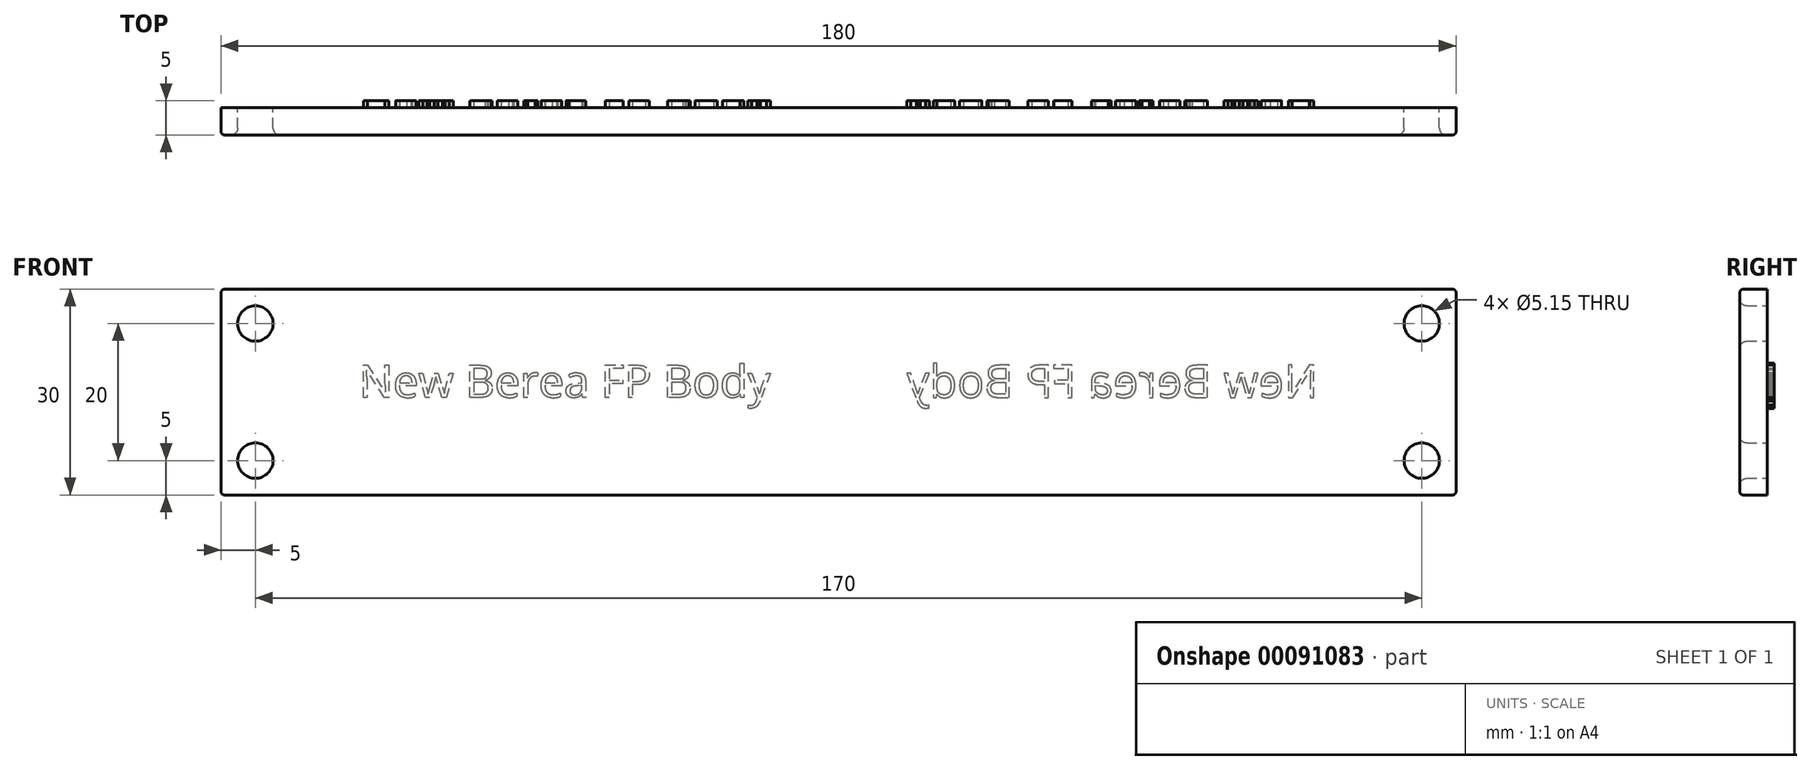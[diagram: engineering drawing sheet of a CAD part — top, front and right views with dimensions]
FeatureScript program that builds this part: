
annotation { "Feature Type Name" : "Feature", "Feature Type Description" : "" }
export const myFeature = defineFeature(function(context is Context, id is Id, definition is map)
    precondition{}
    {
        {
            var Q0;
            Q0=qCreatedBy(makeId("Front.planeOp"),FACE);
            var sketch = newSketch(context, id + "F0", { "sketchPlane" : qUnion([Q0])});
            skLineSegment(sketch, "E0.bottom", {"start": v(-90, -15) * mm, "end": v(90, -15) * mm});
            skLineSegment(sketch, "E0.top", {"start": v(-90, 15) * mm, "end": v(90, 15) * mm});
            skLineSegment(sketch, "E0.left", {"start": v(-90, -15) * mm, "end": v(-90, 15) * mm});
            skLineSegment(sketch, "E0.right", {"start": v(90, -15) * mm, "end": v(90, 15) * mm});
            skPoint(sketch, "E0.middle", {"position": v(0, 0) * mm});
            skCircle(sketch, "E1", {"center": v(-85, 10) * mm, "radius": 2.58 * mm});
            skPoint(sketch, "E2.start.orphan", {"position": v(-90, 0) * mm});
            skPoint(sketch, "E3.orphan", {"position": v(0, 15) * mm});
            skPoint(sketch, "E4.end.orphan", {"position": v(0, -15) * mm});
            skLineSegment(sketch, "E5", {"start": v(-90, 0) * mm, "end": v(0, 0) * mm, "construction": true});
            skLineSegment(sketch, "E6", {"start": v(0, 15) * mm, "end": v(0, -15) * mm, "construction": true});
            skCircle(sketch, "E7.MirrorC", {"center": v(-85, -10) * mm, "radius": 2.58 * mm});
            skCircle(sketch, "E8.MirrorC", {"center": v(85, 10) * mm, "radius": 2.58 * mm});
            skCircle(sketch, "E9.MirrorC", {"center": v(85, -10) * mm, "radius": 2.58 * mm});
            skSolve(sketch);
        }
        {
            var Q0;
            Q0=makeQuery(id+"F0.imprint","IMPRINT",FACE,{"disambiguationData":[TD([[makeQuery(id+"F0.imprint","IMPRINT",EDGE,{"derivedFrom":sQuery(id+"F0.wireOp",EDGE,"E0.bottom")}),1.0]])]});
            extrude(context, id + "F1", {"entities" : qUnion([Q0]), "depth" : 4 * mm});
        }
        {
            var Q0;
            Q0=makeQuery(id+"F1.opExtrude","CAP_EDGE",EDGE,{"disambiguationData":[OSD([sQuery(id+"F0.wireOp",EDGE,"E1")])],"isStart":false});
            var Q1;
            Q1=makeQuery(id+"F1.opExtrude","CAP_EDGE",EDGE,{"disambiguationData":[OSD([sQuery(id+"F0.wireOp",EDGE,"f5b72a5b-8583-449a-bdbf-9ac5a681e1fd0.MirrorC")])],"isStart":false});
            var Q2;
            Q2=makeQuery(id+"F1.opExtrude","CAP_EDGE",EDGE,{"disambiguationData":[OSD([sQuery(id+"F0.wireOp",EDGE,"2623e306-60f4-4522-aa65-1e3e8c2cf5b60.MirrorC")])],"isStart":false});
            var Q3;
            Q3=makeQuery(id+"F1.opExtrude","CAP_EDGE",EDGE,{"disambiguationData":[OSD([sQuery(id+"F0.wireOp",EDGE,"be81a34d-1d50-4ce7-a7a8-4484a1701fac0.MirrorC")])],"isStart":false});
            var Q4;
            Q4=makeQuery(id+"F1.opExtrude","CAP_EDGE",EDGE,{"disambiguationData":[OSD([sQuery(id+"F0.wireOp",EDGE,"E7.MirrorC")])],"isStart":false});
            var Q5;
            Q5=makeQuery(id+"F1.opExtrude","CAP_EDGE",EDGE,{"disambiguationData":[OSD([sQuery(id+"F0.wireOp",EDGE,"E8.MirrorC")])],"isStart":false});
            var Q6;
            Q6=makeQuery(id+"F1.opExtrude","CAP_EDGE",EDGE,{"disambiguationData":[OSD([sQuery(id+"F0.wireOp",EDGE,"E9.MirrorC")])],"isStart":false});
            fillet(context, id + "F2", {"entities" : qUnion([Q0, Q1, Q2, Q3, Q4, Q5, Q6]), "radius" : 1 * mm, "tangentPropagation" : true, "allowEdgeOverflow" : false});
        }
        {
            var Q0;
            Q0=makeQuery(id+"F1.opExtrude","CAP_EDGE",EDGE,{"disambiguationData":[OSD([sQuery(id+"F0.wireOp",EDGE,"E0.top")])],"isStart":false});
            var Q1;
            Q1=makeQuery(id+"F1.opExtrude","CAP_EDGE",EDGE,{"disambiguationData":[OSD([sQuery(id+"F0.wireOp",EDGE,"E0.left")])],"isStart":false});
            var Q2;
            Q2=makeQuery(id+"F1.opExtrude","CAP_EDGE",EDGE,{"disambiguationData":[OSD([sQuery(id+"F0.wireOp",EDGE,"E0.bottom")])],"isStart":false});
            var Q3;
            Q3=makeQuery(id+"F1.opExtrude","CAP_EDGE",EDGE,{"disambiguationData":[OSD([sQuery(id+"F0.wireOp",EDGE,"E0.right")])],"isStart":false});
            var Q4;
            Q4=makeQuery(id+"F1.opExtrude","SWEPT_EDGE",EDGE,{"disambiguationData":[OSD([sQuery(id+"F0.wireOp",EDGE,"E0.top"),sQuery(id+"F0.wireOp",EDGE,"E0.left")])]});
            var Q5;
            Q5=makeQuery(id+"F1.opExtrude","SWEPT_EDGE",EDGE,{"disambiguationData":[OSD([sQuery(id+"F0.wireOp",EDGE,"E0.bottom"),sQuery(id+"F0.wireOp",EDGE,"E0.left")])]});
            var Q6;
            Q6=makeQuery(id+"F1.opExtrude","SWEPT_EDGE",EDGE,{"disambiguationData":[OSD([sQuery(id+"F0.wireOp",EDGE,"E0.top"),sQuery(id+"F0.wireOp",EDGE,"E0.right")])]});
            var Q7;
            Q7=makeQuery(id+"F1.opExtrude","SWEPT_EDGE",EDGE,{"disambiguationData":[OSD([sQuery(id+"F0.wireOp",EDGE,"E0.bottom"),sQuery(id+"F0.wireOp",EDGE,"E0.right")])]});
            fillet(context, id + "F3", {"entities" : qUnion([Q0, Q1, Q2, Q3, Q4, Q5, Q6, Q7]), "radius" : .5 * mm, "tangentPropagation" : true, "allowEdgeOverflow" : false});
        }
        {
            var Q0;
            Q0=makeQuery(id+"F1.opExtrude","CAP_FACE",FACE,{"disambiguationData":[OSD([sQuery(id+"F0.wireOp",EDGE,"E0.bottom"),sQuery(id+"F0.wireOp",EDGE,"E0.top"),sQuery(id+"F0.wireOp",EDGE,"E0.left"),sQuery(id+"F0.wireOp",EDGE,"E0.right"),sQuery(id+"F0.wireOp",EDGE,"E1"),sQuery(id+"F0.wireOp",EDGE,"E7.MirrorC"),sQuery(id+"F0.wireOp",EDGE,"E8.MirrorC"),sQuery(id+"F0.wireOp",EDGE,"E9.MirrorC")])],"isStart":true});
            var sketch = newSketch(context, id + "F4", { "sketchPlane" : qUnion([Q0])});
            skText(sketch, "E10", { "text": "New Berea FP Body\n", "fontName": "OpenSans-Regular.ttf"});
            skLineSegment(sketch, "E11", {"start": v(0, 15) * mm, "end": v(0, -15) * mm, "construction": true});
            const initialGuessF4  = {"E10": [-0.06991, -0.00078, 1, 0, 0.00475]};
            skSetInitialGuess(sketch, initialGuessF4);
            skSolve(sketch);
        }
        {
            var Q0;
            Q0=qSketchRegion(id+"F4",true);
            extrude(context, id + "F5", {"entities" : qUnion([Q0]), "operationType" : NewBodyOperationType.ADD, "depth" : 1 * mm});
        }
        {
            var Q0;
            Q0=makeQuery(id+"F1.opExtrude","SWEPT_BODY",BODY,{"disambiguationData":[OSD([sQuery(id+"F0.wireOp",EDGE,"E0.bottom"),sQuery(id+"F0.wireOp",EDGE,"E0.top"),sQuery(id+"F0.wireOp",EDGE,"E0.left"),sQuery(id+"F0.wireOp",EDGE,"E0.right"),sQuery(id+"F0.wireOp",EDGE,"E1"),sQuery(id+"F0.wireOp",EDGE,"E7.MirrorC"),sQuery(id+"F0.wireOp",EDGE,"E8.MirrorC"),sQuery(id+"F0.wireOp",EDGE,"E9.MirrorC")])]});
            var Q1;
            Q1=makeQuery(id+"F5.opExtrude","SWEPT_FACE",FACE,{"disambiguationData":[OSD([sQuery(id+"F4.wireOp",EDGE,"E10.sketch_text.stroke-94")])]});
            var Q2;
            Q2=makeQuery(id+"F5.opExtrude","SWEPT_FACE",FACE,{"disambiguationData":[OSD([sQuery(id+"F4.wireOp",EDGE,"E10.sketch_text.stroke-169")])]});
            var Q3;
            Q3=makeQuery(id+"F5.opExtrude","SWEPT_FACE",FACE,{"disambiguationData":[OSD([sQuery(id+"F4.wireOp",EDGE,"E10.sketch_text.stroke-185")])]});
            var Q4;
            Q4=makeQuery(id+"F5.opExtrude","SWEPT_FACE",FACE,{"disambiguationData":[OSD([sQuery(id+"F4.wireOp",EDGE,"E10.sketch_text.stroke-125")])]});
            var Q5;
            Q5=makeQuery(id+"F5.opExtrude","SWEPT_FACE",FACE,{"disambiguationData":[OSD([sQuery(id+"F4.wireOp",EDGE,"E10.sketch_text.stroke-155")])]});
            var Q6;
            Q6=makeQuery(id+"F5.opExtrude","SWEPT_FACE",FACE,{"disambiguationData":[OSD([sQuery(id+"F4.wireOp",EDGE,"E10.sketch_text.stroke-65")])]});
            var Q7;
            Q7=makeQuery(id+"F5.opExtrude","SWEPT_FACE",FACE,{"disambiguationData":[OSD([sQuery(id+"F4.wireOp",EDGE,"E10.sketch_text.stroke-81")])]});
            var Q8;
            Q8=makeQuery(id+"F5.opExtrude","SWEPT_FACE",FACE,{"disambiguationData":[OSD([sQuery(id+"F4.wireOp",EDGE,"E10.sketch_text.stroke-67")])]});
            var Q9;
            Q9=makeQuery(id+"F5.opExtrude","SWEPT_FACE",FACE,{"disambiguationData":[OSD([sQuery(id+"F4.wireOp",EDGE,"E10.sketch_text.stroke-99")])]});
            var Q10;
            Q10=makeQuery(id+"F5.opExtrude","SWEPT_FACE",FACE,{"disambiguationData":[OSD([sQuery(id+"F4.wireOp",EDGE,"E10.sketch_text.stroke-127")])]});
            var Q11;
            Q11=makeQuery(id+"F5.opExtrude","SWEPT_FACE",FACE,{"disambiguationData":[OSD([sQuery(id+"F4.wireOp",EDGE,"E10.sketch_text.stroke-10")])]});
            var Q12;
            Q12=makeQuery(id+"F5.opExtrude","CAP_FACE",FACE,{"disambiguationData":[OSD([sQuery(id+"F4.wireOp",EDGE,"E10.sketch_text.stroke-9"),sQuery(id+"F4.wireOp",EDGE,"E10.sketch_text.stroke-10"),sQuery(id+"F4.wireOp",EDGE,"E10.sketch_text.stroke-11"),sQuery(id+"F4.wireOp",EDGE,"E10.sketch_text.stroke-12")])],"isStart":false});
            var Q13;
            Q13=makeQuery(id+"F5.opExtrude","SWEPT_FACE",FACE,{"disambiguationData":[OSD([sQuery(id+"F4.wireOp",EDGE,"E10.sketch_text.stroke-154")])]});
            var Q14;
            Q14=makeQuery(id+"F5.opExtrude","SWEPT_FACE",FACE,{"disambiguationData":[OSD([sQuery(id+"F4.wireOp",EDGE,"E10.sketch_text.stroke-1")])]});
            var Q15;
            Q15=makeQuery(id+"F5.opExtrude","CAP_FACE",FACE,{"disambiguationData":[OSD([sQuery(id+"F4.wireOp",EDGE,"E10.sketch_text.stroke-124"),sQuery(id+"F4.wireOp",EDGE,"E10.sketch_text.stroke-125"),sQuery(id+"F4.wireOp",EDGE,"E10.sketch_text.stroke-126"),sQuery(id+"F4.wireOp",EDGE,"E10.sketch_text.stroke-127"),sQuery(id+"F4.wireOp",EDGE,"E10.sketch_text.stroke-128"),sQuery(id+"F4.wireOp",EDGE,"E10.sketch_text.stroke-129"),sQuery(id+"F4.wireOp",EDGE,"E10.sketch_text.stroke-130"),sQuery(id+"F4.wireOp",EDGE,"E10.sketch_text.stroke-131"),sQuery(id+"F4.wireOp",EDGE,"E10.sketch_text.stroke-132"),sQuery(id+"F4.wireOp",EDGE,"E10.sketch_text.stroke-133"),sQuery(id+"F4.wireOp",EDGE,"E10.sketch_text.stroke-134"),sQuery(id+"F4.wireOp",EDGE,"E10.sketch_text.stroke-135"),sQuery(id+"F4.wireOp",EDGE,"E10.sketch_text.stroke-136"),sQuery(id+"F4.wireOp",EDGE,"E10.sketch_text.stroke-137"),sQuery(id+"F4.wireOp",EDGE,"E10.sketch_text.stroke-138")])],"isStart":false});
            var Q16;
            Q16=makeQuery(id+"F5.opExtrude","CAP_FACE",FACE,{"disambiguationData":[OSD([sQuery(id+"F4.wireOp",EDGE,"E10.sketch_text.stroke-34"),sQuery(id+"F4.wireOp",EDGE,"E10.sketch_text.stroke-35"),sQuery(id+"F4.wireOp",EDGE,"E10.sketch_text.stroke-36"),sQuery(id+"F4.wireOp",EDGE,"E10.sketch_text.stroke-37"),sQuery(id+"F4.wireOp",EDGE,"E10.sketch_text.stroke-38"),sQuery(id+"F4.wireOp",EDGE,"E10.sketch_text.stroke-39"),sQuery(id+"F4.wireOp",EDGE,"E10.sketch_text.stroke-40"),sQuery(id+"F4.wireOp",EDGE,"E10.sketch_text.stroke-41"),sQuery(id+"F4.wireOp",EDGE,"E10.sketch_text.stroke-42"),sQuery(id+"F4.wireOp",EDGE,"E10.sketch_text.stroke-43"),sQuery(id+"F4.wireOp",EDGE,"E10.sketch_text.stroke-44"),sQuery(id+"F4.wireOp",EDGE,"E10.sketch_text.stroke-45"),sQuery(id+"F4.wireOp",EDGE,"E10.sketch_text.stroke-46"),sQuery(id+"F4.wireOp",EDGE,"E10.sketch_text.stroke-47"),sQuery(id+"F4.wireOp",EDGE,"E10.sketch_text.stroke-48"),sQuery(id+"F4.wireOp",EDGE,"E10.sketch_text.stroke-49"),sQuery(id+"F4.wireOp",EDGE,"E10.sketch_text.stroke-50"),sQuery(id+"F4.wireOp",EDGE,"E10.sketch_text.stroke-51"),sQuery(id+"F4.wireOp",EDGE,"E10.sketch_text.stroke-52"),sQuery(id+"F4.wireOp",EDGE,"E10.sketch_text.stroke-53"),sQuery(id+"F4.wireOp",EDGE,"E10.sketch_text.stroke-54"),sQuery(id+"F4.wireOp",EDGE,"E10.sketch_text.stroke-55"),sQuery(id+"F4.wireOp",EDGE,"E10.sketch_text.stroke-56"),sQuery(id+"F4.wireOp",EDGE,"E10.sketch_text.stroke-57"),sQuery(id+"F4.wireOp",EDGE,"E10.sketch_text.stroke-58"),sQuery(id+"F4.wireOp",EDGE,"E10.sketch_text.stroke-59"),sQuery(id+"F4.wireOp",EDGE,"E10.sketch_text.stroke-60")])],"isStart":false});
            var Q17;
            Q17=makeQuery(id+"F5.opExtrude","SWEPT_FACE",FACE,{"disambiguationData":[OSD([sQuery(id+"F4.wireOp",EDGE,"E10.sketch_text.stroke-50")])]});
            var Q18;
            Q18=makeQuery(id+"F5.opExtrude","SWEPT_FACE",FACE,{"disambiguationData":[OSD([sQuery(id+"F4.wireOp",EDGE,"E10.sketch_text.stroke-2")])]});
            var Q19;
            Q19=makeQuery(id+"F5.opExtrude","SWEPT_FACE",FACE,{"disambiguationData":[OSD([sQuery(id+"F4.wireOp",EDGE,"E10.sketch_text.stroke-3")])]});
            var Q20;
            Q20=makeQuery(id+"F5.opExtrude","SWEPT_FACE",FACE,{"disambiguationData":[OSD([sQuery(id+"F4.wireOp",EDGE,"E10.sketch_text.stroke-5")])]});
            var Q21;
            Q21=makeQuery(id+"F5.opExtrude","SWEPT_FACE",FACE,{"disambiguationData":[OSD([sQuery(id+"F4.wireOp",EDGE,"E10.sketch_text.stroke-8")])]});
            var Q22;
            Q22=makeQuery(id+"F5.opExtrude","SWEPT_FACE",FACE,{"disambiguationData":[OSD([sQuery(id+"F4.wireOp",EDGE,"E10.sketch_text.stroke-98")])]});
            var Q23;
            Q23=makeQuery(id+"F5.opExtrude","SWEPT_FACE",FACE,{"disambiguationData":[OSD([sQuery(id+"F4.wireOp",EDGE,"E10.sketch_text.stroke-66")])]});
            var Q24;
            Q24=makeQuery(id+"F5.opExtrude","SWEPT_FACE",FACE,{"disambiguationData":[OSD([sQuery(id+"F4.wireOp",EDGE,"E10.sketch_text.stroke-153")])]});
            var Q25;
            Q25=makeQuery(id+"F5.opExtrude","SWEPT_FACE",FACE,{"disambiguationData":[OSD([sQuery(id+"F4.wireOp",EDGE,"E10.sketch_text.stroke-126")])]});
            var Q26;
            Q26=makeQuery(id+"F5.opExtrude","SWEPT_FACE",FACE,{"disambiguationData":[OSD([sQuery(id+"F4.wireOp",EDGE,"E10.sketch_text.stroke-183")])]});
            var Q27;
            Q27=makeQuery(id+"F5.opExtrude","SWEPT_FACE",FACE,{"disambiguationData":[OSD([sQuery(id+"F4.wireOp",EDGE,"E10.sketch_text.stroke-109")])]});
            var Q28;
            Q28=makeQuery(id+"F5.opExtrude","SWEPT_FACE",FACE,{"disambiguationData":[OSD([sQuery(id+"F4.wireOp",EDGE,"E10.sketch_text.stroke-186")])]});
            var Q29;
            Q29=makeQuery(id+"F5.opExtrude","SWEPT_FACE",FACE,{"disambiguationData":[OSD([sQuery(id+"F4.wireOp",EDGE,"E10.sketch_text.stroke-79")])]});
            var Q30;
            Q30=makeQuery(id+"F5.opExtrude","SWEPT_FACE",FACE,{"disambiguationData":[OSD([sQuery(id+"F4.wireOp",EDGE,"E10.sketch_text.stroke-110")])]});
            var Q31;
            Q31=makeQuery(id+"F5.opExtrude","SWEPT_FACE",FACE,{"disambiguationData":[OSD([sQuery(id+"F4.wireOp",EDGE,"E10.sketch_text.stroke-38")])]});
            var Q32;
            Q32=makeQuery(id+"F5.opExtrude","SWEPT_FACE",FACE,{"disambiguationData":[OSD([sQuery(id+"F4.wireOp",EDGE,"E10.sketch_text.stroke-24")])]});
            var Q33;
            Q33=makeQuery(id+"F5.opExtrude","SWEPT_FACE",FACE,{"disambiguationData":[OSD([sQuery(id+"F4.wireOp",EDGE,"E10.sketch_text.stroke-12")])]});
            var Q34;
            Q34=makeQuery(id+"F5.opExtrude","SWEPT_FACE",FACE,{"disambiguationData":[OSD([sQuery(id+"F4.wireOp",EDGE,"E10.sketch_text.stroke-100")])]});
            var Q35;
            Q35=makeQuery(id+"F5.opExtrude","SWEPT_FACE",FACE,{"disambiguationData":[OSD([sQuery(id+"F4.wireOp",EDGE,"E10.sketch_text.stroke-158")])]});
            var Q36;
            Q36=makeQuery(id+"F5.opExtrude","SWEPT_FACE",FACE,{"disambiguationData":[OSD([sQuery(id+"F4.wireOp",EDGE,"E10.sketch_text.stroke-142")])]});
            var Q37;
            Q37=makeQuery(id+"F5.opExtrude","SWEPT_FACE",FACE,{"disambiguationData":[OSD([sQuery(id+"F4.wireOp",EDGE,"E10.sketch_text.stroke-54")])]});
            var Q38;
            Q38=makeQuery(id+"F5.opExtrude","SWEPT_FACE",FACE,{"disambiguationData":[OSD([sQuery(id+"F4.wireOp",EDGE,"E10.sketch_text.stroke-25")])]});
            var Q39;
            Q39=makeQuery(id+"F5.opExtrude","SWEPT_FACE",FACE,{"disambiguationData":[OSD([sQuery(id+"F4.wireOp",EDGE,"E10.sketch_text.stroke-101")])]});
            var Q40;
            Q40=makeQuery(id+"F5.opExtrude","SWEPT_FACE",FACE,{"disambiguationData":[OSD([sQuery(id+"F4.wireOp",EDGE,"E10.sketch_text.stroke-69")])]});
            var Q41;
            Q41=makeQuery(id+"F5.opExtrude","SWEPT_FACE",FACE,{"disambiguationData":[OSD([sQuery(id+"F4.wireOp",EDGE,"E10.sketch_text.stroke-159")])]});
            var Q42;
            Q42=makeQuery(id+"F5.opExtrude","SWEPT_FACE",FACE,{"disambiguationData":[OSD([sQuery(id+"F4.wireOp",EDGE,"E10.sketch_text.stroke-85")])]});
            var Q43;
            Q43=makeQuery(id+"F5.opExtrude","SWEPT_FACE",FACE,{"disambiguationData":[OSD([sQuery(id+"F4.wireOp",EDGE,"E10.sketch_text.stroke-173")])]});
            var Q44;
            Q44=makeQuery(id+"F5.opExtrude","SWEPT_FACE",FACE,{"disambiguationData":[OSD([sQuery(id+"F4.wireOp",EDGE,"E10.sketch_text.stroke-40")])]});
            var Q45;
            Q45=makeQuery(id+"F5.opExtrude","SWEPT_FACE",FACE,{"disambiguationData":[OSD([sQuery(id+"F4.wireOp",EDGE,"E10.sketch_text.stroke-102")])]});
            var Q46;
            Q46=makeQuery(id+"F5.opExtrude","SWEPT_FACE",FACE,{"disambiguationData":[OSD([sQuery(id+"F4.wireOp",EDGE,"E10.sketch_text.stroke-86")])]});
            var Q47;
            Q47=makeQuery(id+"F5.opExtrude","SWEPT_FACE",FACE,{"disambiguationData":[OSD([sQuery(id+"F4.wireOp",EDGE,"E10.sketch_text.stroke-130")])]});
            var Q48;
            Q48=makeQuery(id+"F5.opExtrude","SWEPT_FACE",FACE,{"disambiguationData":[OSD([sQuery(id+"F4.wireOp",EDGE,"E10.sketch_text.stroke-103")])]});
            var Q49;
            Q49=makeQuery(id+"F5.opExtrude","SWEPT_FACE",FACE,{"disambiguationData":[OSD([sQuery(id+"F4.wireOp",EDGE,"E10.sketch_text.stroke-87")])]});
            var Q50;
            Q50=makeQuery(id+"F5.opExtrude","SWEPT_FACE",FACE,{"disambiguationData":[OSD([sQuery(id+"F4.wireOp",EDGE,"E10.sketch_text.stroke-145")])]});
            var Q51;
            Q51=makeQuery(id+"F5.opExtrude","SWEPT_FACE",FACE,{"disambiguationData":[OSD([sQuery(id+"F4.wireOp",EDGE,"E10.sketch_text.stroke-131")])]});
            var Q52;
            Q52=makeQuery(id+"F5.opExtrude","SWEPT_FACE",FACE,{"disambiguationData":[OSD([sQuery(id+"F4.wireOp",EDGE,"E10.sketch_text.stroke-28")])]});
            var Q53;
            Q53=makeQuery(id+"F5.opExtrude","SWEPT_FACE",FACE,{"disambiguationData":[OSD([sQuery(id+"F4.wireOp",EDGE,"E10.sketch_text.stroke-14")])]});
            var Q54;
            Q54=makeQuery(id+"F5.opExtrude","SWEPT_FACE",FACE,{"disambiguationData":[OSD([sQuery(id+"F4.wireOp",EDGE,"E10.sketch_text.stroke-88")])]});
            var Q55;
            Q55=makeQuery(id+"F5.opExtrude","SWEPT_FACE",FACE,{"disambiguationData":[OSD([sQuery(id+"F4.wireOp",EDGE,"E10.sketch_text.stroke-162")])]});
            var Q56;
            Q56=makeQuery(id+"F5.opExtrude","SWEPT_FACE",FACE,{"disambiguationData":[OSD([sQuery(id+"F4.wireOp",EDGE,"E10.sketch_text.stroke-176")])]});
            var Q57;
            Q57=makeQuery(id+"F5.opExtrude","SWEPT_FACE",FACE,{"disambiguationData":[OSD([sQuery(id+"F4.wireOp",EDGE,"E10.sketch_text.stroke-73")])]});
            var Q58;
            Q58=makeQuery(id+"F5.opExtrude","SWEPT_FACE",FACE,{"disambiguationData":[OSD([sQuery(id+"F4.wireOp",EDGE,"E10.sketch_text.stroke-59")])]});
            var Q59;
            Q59=makeQuery(id+"F5.opExtrude","SWEPT_FACE",FACE,{"disambiguationData":[OSD([sQuery(id+"F4.wireOp",EDGE,"E10.sketch_text.stroke-133")])]});
            var Q60;
            Q60=makeQuery(id+"F5.opExtrude","SWEPT_FACE",FACE,{"disambiguationData":[OSD([sQuery(id+"F4.wireOp",EDGE,"E10.sketch_text.stroke-119")])]});
            var Q61;
            Q61=makeQuery(id+"F5.opExtrude","SWEPT_FACE",FACE,{"disambiguationData":[OSD([sQuery(id+"F4.wireOp",EDGE,"E10.sketch_text.stroke-74")])]});
            var Q62;
            Q62=makeQuery(id+"F5.opExtrude","SWEPT_FACE",FACE,{"disambiguationData":[OSD([sQuery(id+"F4.wireOp",EDGE,"E10.sketch_text.stroke-44")])]});
            var Q63;
            Q63=makeQuery(id+"F5.opExtrude","SWEPT_FACE",FACE,{"disambiguationData":[OSD([sQuery(id+"F4.wireOp",EDGE,"E10.sketch_text.stroke-120")])]});
            var Q64;
            Q64=makeQuery(id+"F5.opExtrude","SWEPT_FACE",FACE,{"disambiguationData":[OSD([sQuery(id+"F4.wireOp",EDGE,"E10.sketch_text.stroke-90")])]});
            var Q65;
            Q65=makeQuery(id+"F5.opExtrude","SWEPT_FACE",FACE,{"disambiguationData":[OSD([sQuery(id+"F4.wireOp",EDGE,"E10.sketch_text.stroke-178")])]});
            var Q66;
            Q66=makeQuery(id+"F5.opExtrude","SWEPT_FACE",FACE,{"disambiguationData":[OSD([sQuery(id+"F4.wireOp",EDGE,"E10.sketch_text.stroke-45")])]});
            var Q67;
            Q67=makeQuery(id+"F5.opExtrude","SWEPT_FACE",FACE,{"disambiguationData":[OSD([sQuery(id+"F4.wireOp",EDGE,"E10.sketch_text.stroke-31")])]});
            var Q68;
            Q68=makeQuery(id+"F5.opExtrude","SWEPT_FACE",FACE,{"disambiguationData":[OSD([sQuery(id+"F4.wireOp",EDGE,"E10.sketch_text.stroke-135")])]});
            var Q69;
            Q69=makeQuery(id+"F5.opExtrude","SWEPT_FACE",FACE,{"disambiguationData":[OSD([sQuery(id+"F4.wireOp",EDGE,"E10.sketch_text.stroke-179")])]});
            var Q70;
            Q70=makeQuery(id+"F5.opExtrude","SWEPT_FACE",FACE,{"disambiguationData":[OSD([sQuery(id+"F4.wireOp",EDGE,"E10.sketch_text.stroke-165")])]});
            var Q71;
            Q71=makeQuery(id+"F5.opExtrude","SWEPT_FACE",FACE,{"disambiguationData":[OSD([sQuery(id+"F4.wireOp",EDGE,"E10.sketch_text.stroke-149")])]});
            var Q72;
            Q72=makeQuery(id+"F5.opExtrude","SWEPT_FACE",FACE,{"disambiguationData":[OSD([sQuery(id+"F4.wireOp",EDGE,"E10.sketch_text.stroke-136")])]});
            var Q73;
            Q73=makeQuery(id+"F5.opExtrude","SWEPT_FACE",FACE,{"disambiguationData":[OSD([sQuery(id+"F4.wireOp",EDGE,"E10.sketch_text.stroke-122")])]});
            var Q74;
            Q74=makeQuery(id+"F5.opExtrude","SWEPT_FACE",FACE,{"disambiguationData":[OSD([sQuery(id+"F4.wireOp",EDGE,"E10.sketch_text.stroke-106")])]});
            var Q75;
            Q75=makeQuery(id+"F5.opExtrude","SWEPT_FACE",FACE,{"disambiguationData":[OSD([sQuery(id+"F4.wireOp",EDGE,"E10.sketch_text.stroke-180")])]});
            var Q76;
            Q76=makeQuery(id+"F5.opExtrude","SWEPT_FACE",FACE,{"disambiguationData":[OSD([sQuery(id+"F4.wireOp",EDGE,"E10.sketch_text.stroke-166")])]});
            var Q77;
            Q77=makeQuery(id+"F5.opExtrude","SWEPT_FACE",FACE,{"disambiguationData":[OSD([sQuery(id+"F4.wireOp",EDGE,"E10.sketch_text.stroke-150")])]});
            var Q78;
            Q78=makeQuery(id+"F5.opExtrude","SWEPT_FACE",FACE,{"disambiguationData":[OSD([sQuery(id+"F4.wireOp",EDGE,"E10.sketch_text.stroke-76")])]});
            var Q79;
            Q79=makeQuery(id+"F5.opExtrude","SWEPT_FACE",FACE,{"disambiguationData":[OSD([sQuery(id+"F4.wireOp",EDGE,"E10.sketch_text.stroke-32")])]});
            var Q80;
            Q80=makeQuery(id+"F5.opExtrude","SWEPT_FACE",FACE,{"disambiguationData":[OSD([sQuery(id+"F4.wireOp",EDGE,"E10.sketch_text.stroke-181")])]});
            var Q81;
            Q81=makeQuery(id+"F5.opExtrude","SWEPT_FACE",FACE,{"disambiguationData":[OSD([sQuery(id+"F4.wireOp",EDGE,"E10.sketch_text.stroke-47")])]});
            var Q82;
            Q82=makeQuery(id+"F5.opExtrude","SWEPT_FACE",FACE,{"disambiguationData":[OSD([sQuery(id+"F4.wireOp",EDGE,"E10.sketch_text.stroke-123")])]});
            var Q83;
            Q83=makeQuery(id+"F5.opExtrude","SWEPT_FACE",FACE,{"disambiguationData":[OSD([sQuery(id+"F4.wireOp",EDGE,"E10.sketch_text.stroke-107")])]});
            var Q84;
            Q84=makeQuery(id+"F5.opExtrude","SWEPT_FACE",FACE,{"disambiguationData":[OSD([sQuery(id+"F4.wireOp",EDGE,"E10.sketch_text.stroke-48")])]});
            var Q85;
            Q85=makeQuery(id+"F5.opExtrude","SWEPT_FACE",FACE,{"disambiguationData":[OSD([sQuery(id+"F4.wireOp",EDGE,"E10.sketch_text.stroke-124")])]});
            var Q86;
            Q86=makeQuery(id+"F5.opExtrude","SWEPT_FACE",FACE,{"disambiguationData":[OSD([sQuery(id+"F4.wireOp",EDGE,"E10.sketch_text.stroke-108")])]});
            var Q87;
            Q87=makeQuery(id+"F5.opExtrude","CAP_FACE",FACE,{"disambiguationData":[OSD([sQuery(id+"F4.wireOp",EDGE,"E10.sketch_text.stroke-139"),sQuery(id+"F4.wireOp",EDGE,"E10.sketch_text.stroke-140"),sQuery(id+"F4.wireOp",EDGE,"E10.sketch_text.stroke-141"),sQuery(id+"F4.wireOp",EDGE,"E10.sketch_text.stroke-142"),sQuery(id+"F4.wireOp",EDGE,"E10.sketch_text.stroke-143"),sQuery(id+"F4.wireOp",EDGE,"E10.sketch_text.stroke-144"),sQuery(id+"F4.wireOp",EDGE,"E10.sketch_text.stroke-145"),sQuery(id+"F4.wireOp",EDGE,"E10.sketch_text.stroke-146"),sQuery(id+"F4.wireOp",EDGE,"E10.sketch_text.stroke-147"),sQuery(id+"F4.wireOp",EDGE,"E10.sketch_text.stroke-148"),sQuery(id+"F4.wireOp",EDGE,"E10.sketch_text.stroke-149"),sQuery(id+"F4.wireOp",EDGE,"E10.sketch_text.stroke-150"),sQuery(id+"F4.wireOp",EDGE,"E10.sketch_text.stroke-151"),sQuery(id+"F4.wireOp",EDGE,"E10.sketch_text.stroke-152"),sQuery(id+"F4.wireOp",EDGE,"E10.sketch_text.stroke-153"),sQuery(id+"F4.wireOp",EDGE,"E10.sketch_text.stroke-154"),sQuery(id+"F4.wireOp",EDGE,"E10.sketch_text.stroke-155"),sQuery(id+"F4.wireOp",EDGE,"E10.sketch_text.stroke-156"),sQuery(id+"F4.wireOp",EDGE,"E10.sketch_text.stroke-157"),sQuery(id+"F4.wireOp",EDGE,"E10.sketch_text.stroke-158"),sQuery(id+"F4.wireOp",EDGE,"E10.sketch_text.stroke-159"),sQuery(id+"F4.wireOp",EDGE,"E10.sketch_text.stroke-160"),sQuery(id+"F4.wireOp",EDGE,"E10.sketch_text.stroke-161"),sQuery(id+"F4.wireOp",EDGE,"E10.sketch_text.stroke-162"),sQuery(id+"F4.wireOp",EDGE,"E10.sketch_text.stroke-163"),sQuery(id+"F4.wireOp",EDGE,"E10.sketch_text.stroke-164"),sQuery(id+"F4.wireOp",EDGE,"E10.sketch_text.stroke-165")])],"isStart":false});
            var Q88;
            Q88=makeQuery(id+"F5.opExtrude","CAP_FACE",FACE,{"disambiguationData":[OSD([sQuery(id+"F4.wireOp",EDGE,"E10.sketch_text.stroke-21"),sQuery(id+"F4.wireOp",EDGE,"E10.sketch_text.stroke-22"),sQuery(id+"F4.wireOp",EDGE,"E10.sketch_text.stroke-23"),sQuery(id+"F4.wireOp",EDGE,"E10.sketch_text.stroke-24"),sQuery(id+"F4.wireOp",EDGE,"E10.sketch_text.stroke-25"),sQuery(id+"F4.wireOp",EDGE,"E10.sketch_text.stroke-26"),sQuery(id+"F4.wireOp",EDGE,"E10.sketch_text.stroke-27"),sQuery(id+"F4.wireOp",EDGE,"E10.sketch_text.stroke-28"),sQuery(id+"F4.wireOp",EDGE,"E10.sketch_text.stroke-29"),sQuery(id+"F4.wireOp",EDGE,"E10.sketch_text.stroke-30"),sQuery(id+"F4.wireOp",EDGE,"E10.sketch_text.stroke-31"),sQuery(id+"F4.wireOp",EDGE,"E10.sketch_text.stroke-32"),sQuery(id+"F4.wireOp",EDGE,"E10.sketch_text.stroke-33")])],"isStart":false});
            var Q89;
            Q89=makeQuery(id+"F5.opExtrude","SWEPT_FACE",FACE,{"disambiguationData":[OSD([sQuery(id+"F4.wireOp",EDGE,"E10.sketch_text.stroke-113")])]});
            var Q90;
            Q90=makeQuery(id+"F5.opExtrude","SWEPT_FACE",FACE,{"disambiguationData":[OSD([sQuery(id+"F4.wireOp",EDGE,"E10.sketch_text.stroke-37")])]});
            var Q91;
            Q91=makeQuery(id+"F5.opExtrude","SWEPT_FACE",FACE,{"disambiguationData":[OSD([sQuery(id+"F4.wireOp",EDGE,"E10.sketch_text.stroke-187")])]});
            var Q92;
            Q92=makeQuery(id+"F5.opExtrude","SWEPT_FACE",FACE,{"disambiguationData":[OSD([sQuery(id+"F4.wireOp",EDGE,"E10.sketch_text.stroke-0")])]});
            var Q93;
            Q93=makeQuery(id+"F5.opExtrude","SWEPT_FACE",FACE,{"disambiguationData":[OSD([sQuery(id+"F4.wireOp",EDGE,"E10.sketch_text.stroke-4")])]});
            var Q94;
            Q94=makeQuery(id+"F5.opExtrude","SWEPT_FACE",FACE,{"disambiguationData":[OSD([sQuery(id+"F4.wireOp",EDGE,"E10.sketch_text.stroke-82")])]});
            var Q95;
            Q95=makeQuery(id+"F5.opExtrude","SWEPT_FACE",FACE,{"disambiguationData":[OSD([sQuery(id+"F4.wireOp",EDGE,"E10.sketch_text.stroke-52")])]});
            var Q96;
            Q96=makeQuery(id+"F5.opExtrude","SWEPT_FACE",FACE,{"disambiguationData":[OSD([sQuery(id+"F4.wireOp",EDGE,"E10.sketch_text.stroke-49")])]});
            var Q97;
            Q97=makeQuery(id+"F5.opExtrude","SWEPT_FACE",FACE,{"disambiguationData":[OSD([sQuery(id+"F4.wireOp",EDGE,"E10.sketch_text.stroke-63")])]});
            var Q98;
            Q98=makeQuery(id+"F5.opExtrude","SWEPT_FACE",FACE,{"disambiguationData":[OSD([sQuery(id+"F4.wireOp",EDGE,"E10.sketch_text.stroke-21")])]});
            var Q99;
            Q99=makeQuery(id+"F5.opExtrude","SWEPT_FACE",FACE,{"disambiguationData":[OSD([sQuery(id+"F4.wireOp",EDGE,"E10.sketch_text.stroke-128")])]});
            var Q100;
            Q100=makeQuery(id+"F5.opExtrude","SWEPT_FACE",FACE,{"disambiguationData":[OSD([sQuery(id+"F4.wireOp",EDGE,"E10.sketch_text.stroke-55")])]});
            var Q101;
            Q101=makeQuery(id+"F5.opExtrude","SWEPT_FACE",FACE,{"disambiguationData":[OSD([sQuery(id+"F4.wireOp",EDGE,"E10.sketch_text.stroke-26")])]});
            var Q102;
            Q102=makeQuery(id+"F5.opExtrude","SWEPT_FACE",FACE,{"disambiguationData":[OSD([sQuery(id+"F4.wireOp",EDGE,"E10.sketch_text.stroke-174")])]});
            var Q103;
            Q103=makeQuery(id+"F5.opExtrude","SWEPT_FACE",FACE,{"disambiguationData":[OSD([sQuery(id+"F4.wireOp",EDGE,"E10.sketch_text.stroke-104")])]});
            var Q104;
            Q104=makeQuery(id+"F5.opExtrude","SWEPT_FACE",FACE,{"disambiguationData":[OSD([sQuery(id+"F4.wireOp",EDGE,"E10.sketch_text.stroke-72")])]});
            var Q105;
            Q105=makeQuery(id+"F5.opExtrude","SWEPT_FACE",FACE,{"disambiguationData":[OSD([sQuery(id+"F4.wireOp",EDGE,"E10.sketch_text.stroke-132")])]});
            var Q106;
            Q106=makeQuery(id+"F5.opExtrude","SWEPT_FACE",FACE,{"disambiguationData":[OSD([sQuery(id+"F4.wireOp",EDGE,"E10.sketch_text.stroke-43")])]});
            var Q107;
            Q107=makeQuery(id+"F5.opExtrude","SWEPT_FACE",FACE,{"disambiguationData":[OSD([sQuery(id+"F4.wireOp",EDGE,"E10.sketch_text.stroke-15")])]});
            var Q108;
            Q108=makeQuery(id+"F5.opExtrude","SWEPT_FACE",FACE,{"disambiguationData":[OSD([sQuery(id+"F4.wireOp",EDGE,"E10.sketch_text.stroke-89")])]});
            var Q109;
            Q109=makeQuery(id+"F5.opExtrude","SWEPT_FACE",FACE,{"disambiguationData":[OSD([sQuery(id+"F4.wireOp",EDGE,"E10.sketch_text.stroke-163")])]});
            var Q110;
            Q110=makeQuery(id+"F5.opExtrude","SWEPT_FACE",FACE,{"disambiguationData":[OSD([sQuery(id+"F4.wireOp",EDGE,"E10.sketch_text.stroke-30")])]});
            var Q111;
            Q111=makeQuery(id+"F5.opExtrude","SWEPT_FACE",FACE,{"disambiguationData":[OSD([sQuery(id+"F4.wireOp",EDGE,"E10.sketch_text.stroke-134")])]});
            var Q112;
            Q112=makeQuery(id+"F5.opExtrude","SWEPT_FACE",FACE,{"disambiguationData":[OSD([sQuery(id+"F4.wireOp",EDGE,"E10.sketch_text.stroke-121")])]});
            var Q113;
            Q113=makeQuery(id+"F5.opExtrude","CAP_FACE",FACE,{"disambiguationData":[OSD([sQuery(id+"F4.wireOp",EDGE,"E10.sketch_text.stroke-105"),sQuery(id+"F4.wireOp",EDGE,"E10.sketch_text.stroke-106"),sQuery(id+"F4.wireOp",EDGE,"E10.sketch_text.stroke-107"),sQuery(id+"F4.wireOp",EDGE,"E10.sketch_text.stroke-108"),sQuery(id+"F4.wireOp",EDGE,"E10.sketch_text.stroke-109"),sQuery(id+"F4.wireOp",EDGE,"E10.sketch_text.stroke-110"),sQuery(id+"F4.wireOp",EDGE,"E10.sketch_text.stroke-111"),sQuery(id+"F4.wireOp",EDGE,"E10.sketch_text.stroke-112"),sQuery(id+"F4.wireOp",EDGE,"E10.sketch_text.stroke-113"),sQuery(id+"F4.wireOp",EDGE,"E10.sketch_text.stroke-114"),sQuery(id+"F4.wireOp",EDGE,"E10.sketch_text.stroke-115"),sQuery(id+"F4.wireOp",EDGE,"E10.sketch_text.stroke-116"),sQuery(id+"F4.wireOp",EDGE,"E10.sketch_text.stroke-117"),sQuery(id+"F4.wireOp",EDGE,"E10.sketch_text.stroke-118"),sQuery(id+"F4.wireOp",EDGE,"E10.sketch_text.stroke-119"),sQuery(id+"F4.wireOp",EDGE,"E10.sketch_text.stroke-120"),sQuery(id+"F4.wireOp",EDGE,"E10.sketch_text.stroke-121"),sQuery(id+"F4.wireOp",EDGE,"E10.sketch_text.stroke-122"),sQuery(id+"F4.wireOp",EDGE,"E10.sketch_text.stroke-123")])],"isStart":false});
            var Q114;
            Q114=makeQuery(id+"F5.opExtrude","SWEPT_FACE",FACE,{"disambiguationData":[OSD([sQuery(id+"F4.wireOp",EDGE,"E10.sketch_text.stroke-92")])]});
            var Q115;
            Q115=makeQuery(id+"F5.opExtrude","SWEPT_FACE",FACE,{"disambiguationData":[OSD([sQuery(id+"F4.wireOp",EDGE,"E10.sketch_text.stroke-46")])]});
            var Q116;
            Q116=makeQuery(id+"F5.opExtrude","CAP_FACE",FACE,{"disambiguationData":[OSD([sQuery(id+"F4.wireOp",EDGE,"E10.sketch_text.stroke-61"),sQuery(id+"F4.wireOp",EDGE,"E10.sketch_text.stroke-62"),sQuery(id+"F4.wireOp",EDGE,"E10.sketch_text.stroke-63"),sQuery(id+"F4.wireOp",EDGE,"E10.sketch_text.stroke-64"),sQuery(id+"F4.wireOp",EDGE,"E10.sketch_text.stroke-65"),sQuery(id+"F4.wireOp",EDGE,"E10.sketch_text.stroke-66"),sQuery(id+"F4.wireOp",EDGE,"E10.sketch_text.stroke-67"),sQuery(id+"F4.wireOp",EDGE,"E10.sketch_text.stroke-68"),sQuery(id+"F4.wireOp",EDGE,"E10.sketch_text.stroke-69"),sQuery(id+"F4.wireOp",EDGE,"E10.sketch_text.stroke-70"),sQuery(id+"F4.wireOp",EDGE,"E10.sketch_text.stroke-71"),sQuery(id+"F4.wireOp",EDGE,"E10.sketch_text.stroke-72"),sQuery(id+"F4.wireOp",EDGE,"E10.sketch_text.stroke-73"),sQuery(id+"F4.wireOp",EDGE,"E10.sketch_text.stroke-74"),sQuery(id+"F4.wireOp",EDGE,"E10.sketch_text.stroke-75"),sQuery(id+"F4.wireOp",EDGE,"E10.sketch_text.stroke-76"),sQuery(id+"F4.wireOp",EDGE,"E10.sketch_text.stroke-77"),sQuery(id+"F4.wireOp",EDGE,"E10.sketch_text.stroke-78"),sQuery(id+"F4.wireOp",EDGE,"E10.sketch_text.stroke-79"),sQuery(id+"F4.wireOp",EDGE,"E10.sketch_text.stroke-80"),sQuery(id+"F4.wireOp",EDGE,"E10.sketch_text.stroke-81"),sQuery(id+"F4.wireOp",EDGE,"E10.sketch_text.stroke-82"),sQuery(id+"F4.wireOp",EDGE,"E10.sketch_text.stroke-83"),sQuery(id+"F4.wireOp",EDGE,"E10.sketch_text.stroke-84"),sQuery(id+"F4.wireOp",EDGE,"E10.sketch_text.stroke-85"),sQuery(id+"F4.wireOp",EDGE,"E10.sketch_text.stroke-86"),sQuery(id+"F4.wireOp",EDGE,"E10.sketch_text.stroke-87"),sQuery(id+"F4.wireOp",EDGE,"E10.sketch_text.stroke-88"),sQuery(id+"F4.wireOp",EDGE,"E10.sketch_text.stroke-89"),sQuery(id+"F4.wireOp",EDGE,"E10.sketch_text.stroke-90"),sQuery(id+"F4.wireOp",EDGE,"E10.sketch_text.stroke-91"),sQuery(id+"F4.wireOp",EDGE,"E10.sketch_text.stroke-92"),sQuery(id+"F4.wireOp",EDGE,"E10.sketch_text.stroke-93"),sQuery(id+"F4.wireOp",EDGE,"E10.sketch_text.stroke-94"),sQuery(id+"F4.wireOp",EDGE,"E10.sketch_text.stroke-95"),sQuery(id+"F4.wireOp",EDGE,"E10.sketch_text.stroke-96"),sQuery(id+"F4.wireOp",EDGE,"E10.sketch_text.stroke-97"),sQuery(id+"F4.wireOp",EDGE,"E10.sketch_text.stroke-98"),sQuery(id+"F4.wireOp",EDGE,"E10.sketch_text.stroke-99"),sQuery(id+"F4.wireOp",EDGE,"E10.sketch_text.stroke-100"),sQuery(id+"F4.wireOp",EDGE,"E10.sketch_text.stroke-101"),sQuery(id+"F4.wireOp",EDGE,"E10.sketch_text.stroke-102"),sQuery(id+"F4.wireOp",EDGE,"E10.sketch_text.stroke-103"),sQuery(id+"F4.wireOp",EDGE,"E10.sketch_text.stroke-104")])],"isStart":false});
            var Q117;
            Q117=makeQuery(id+"F5.opExtrude","SWEPT_FACE",FACE,{"disambiguationData":[OSD([sQuery(id+"F4.wireOp",EDGE,"E10.sketch_text.stroke-33")])]});
            var Q118;
            Q118=makeQuery(id+"F5.opExtrude","SWEPT_FACE",FACE,{"disambiguationData":[OSD([sQuery(id+"F4.wireOp",EDGE,"E10.sketch_text.stroke-93")])]});
            var Q119;
            Q119=makeQuery(id+"F5.opExtrude","SWEPT_FACE",FACE,{"disambiguationData":[OSD([sQuery(id+"F4.wireOp",EDGE,"E10.sketch_text.stroke-34")])]});
            var Q120;
            Q120=makeQuery(id+"F5.opExtrude","SWEPT_FACE",FACE,{"disambiguationData":[OSD([sQuery(id+"F4.wireOp",EDGE,"E10.sketch_text.stroke-152")])]});
            var Q121;
            Q121=makeQuery(id+"F5.opExtrude","SWEPT_FACE",FACE,{"disambiguationData":[OSD([sQuery(id+"F4.wireOp",EDGE,"E10.sketch_text.stroke-51")])]});
            var Q122;
            Q122=makeQuery(id+"F5.opExtrude","SWEPT_FACE",FACE,{"disambiguationData":[OSD([sQuery(id+"F4.wireOp",EDGE,"E10.sketch_text.stroke-6")])]});
            var Q123;
            Q123=makeQuery(id+"F5.opExtrude","SWEPT_FACE",FACE,{"disambiguationData":[OSD([sQuery(id+"F4.wireOp",EDGE,"E10.sketch_text.stroke-7")])]});
            var Q124;
            Q124=makeQuery(id+"F5.opExtrude","SWEPT_FACE",FACE,{"disambiguationData":[OSD([sQuery(id+"F4.wireOp",EDGE,"E10.sketch_text.stroke-156")])]});
            var Q125;
            Q125=makeQuery(id+"F5.opExtrude","SWEPT_FACE",FACE,{"disambiguationData":[OSD([sQuery(id+"F4.wireOp",EDGE,"E10.sketch_text.stroke-112")])]});
            var Q126;
            Q126=makeQuery(id+"F5.boolean.opBoolean","SPLIT",FACE,{"disambiguationData":[TD([makeQuery(id+"F5.opExtrude","SWEPT_FACE",FACE,{"disambiguationData":[OSD([sQuery(id+"F4.wireOp",EDGE,"E10.sketch_text.stroke-182")])]})])],"derivedFrom":makeQuery(id+"F1.opExtrude","CAP_FACE",FACE,{"disambiguationData":[OSD([sQuery(id+"F0.wireOp",EDGE,"E0.bottom"),sQuery(id+"F0.wireOp",EDGE,"E0.top"),sQuery(id+"F0.wireOp",EDGE,"E0.left"),sQuery(id+"F0.wireOp",EDGE,"E0.right"),sQuery(id+"F0.wireOp",EDGE,"E1"),sQuery(id+"F0.wireOp",EDGE,"E7.MirrorC"),sQuery(id+"F0.wireOp",EDGE,"E8.MirrorC"),sQuery(id+"F0.wireOp",EDGE,"E9.MirrorC")])],"isStart":true})});
            var Q127;
            Q127=makeQuery(id+"F5.opExtrude","SWEPT_FACE",FACE,{"disambiguationData":[OSD([sQuery(id+"F4.wireOp",EDGE,"E10.sketch_text.stroke-96")])]});
            var Q128;
            Q128=makeQuery(id+"F5.opExtrude","SWEPT_FACE",FACE,{"disambiguationData":[OSD([sQuery(id+"F4.wireOp",EDGE,"E10.sketch_text.stroke-114")])]});
            var Q129;
            Q129=makeQuery(id+"F5.opExtrude","SWEPT_FACE",FACE,{"disambiguationData":[OSD([sQuery(id+"F4.wireOp",EDGE,"E10.sketch_text.stroke-39")])]});
            var Q130;
            Q130=makeQuery(id+"F5.opExtrude","SWEPT_FACE",FACE,{"disambiguationData":[OSD([sQuery(id+"F4.wireOp",EDGE,"E10.sketch_text.stroke-13")])]});
            var Q131;
            Q131=makeQuery(id+"F5.opExtrude","SWEPT_FACE",FACE,{"disambiguationData":[OSD([sQuery(id+"F4.wireOp",EDGE,"E10.sketch_text.stroke-115")])]});
            var Q132;
            Q132=makeQuery(id+"F5.opExtrude","SWEPT_FACE",FACE,{"disambiguationData":[OSD([sQuery(id+"F4.wireOp",EDGE,"E10.sketch_text.stroke-56")])]});
            var Q133;
            Q133=makeQuery(id+"F5.opExtrude","SWEPT_FACE",FACE,{"disambiguationData":[OSD([sQuery(id+"F4.wireOp",EDGE,"E10.sketch_text.stroke-144")])]});
            var Q134;
            Q134=makeQuery(id+"F5.opExtrude","SWEPT_FACE",FACE,{"disambiguationData":[OSD([sQuery(id+"F4.wireOp",EDGE,"E10.sketch_text.stroke-190")])]});
            var Q135;
            Q135=makeQuery(id+"F5.opExtrude","SWEPT_FACE",FACE,{"disambiguationData":[OSD([sQuery(id+"F4.wireOp",EDGE,"E10.sketch_text.stroke-116")])]});
            var Q136;
            Q136=makeQuery(id+"F5.opExtrude","SWEPT_FACE",FACE,{"disambiguationData":[OSD([sQuery(id+"F4.wireOp",EDGE,"E10.sketch_text.stroke-41")])]});
            var Q137;
            Q137=makeQuery(id+"F5.opExtrude","SWEPT_FACE",FACE,{"disambiguationData":[OSD([sQuery(id+"F4.wireOp",EDGE,"E10.sketch_text.stroke-161")])]});
            var Q138;
            Q138=makeQuery(id+"F5.opExtrude","SWEPT_FACE",FACE,{"disambiguationData":[OSD([sQuery(id+"F4.wireOp",EDGE,"E10.sketch_text.stroke-146")])]});
            var Q139;
            Q139=makeQuery(id+"F5.opExtrude","SWEPT_FACE",FACE,{"disambiguationData":[OSD([sQuery(id+"F4.wireOp",EDGE,"E10.sketch_text.stroke-58")])]});
            var Q140;
            Q140=makeQuery(id+"F5.opExtrude","SWEPT_FACE",FACE,{"disambiguationData":[OSD([sQuery(id+"F4.wireOp",EDGE,"E10.sketch_text.stroke-105")])]});
            var Q141;
            Q141=makeQuery(id+"F5.opExtrude","SWEPT_FACE",FACE,{"disambiguationData":[OSD([sQuery(id+"F4.wireOp",EDGE,"E10.sketch_text.stroke-177")])]});
            var Q142;
            Q142=makeQuery(id+"F5.opExtrude","SWEPT_FACE",FACE,{"disambiguationData":[OSD([sQuery(id+"F4.wireOp",EDGE,"E10.sketch_text.stroke-77")])]});
            var Q143;
            Q143=makeQuery(id+"F5.opExtrude","SWEPT_FACE",FACE,{"disambiguationData":[OSD([sQuery(id+"F4.wireOp",EDGE,"E10.sketch_text.stroke-138")])]});
            var Q144;
            Q144=makeQuery(id+"F5.opExtrude","SWEPT_FACE",FACE,{"disambiguationData":[OSD([sQuery(id+"F4.wireOp",EDGE,"E10.sketch_text.stroke-111")])]});
            var Q145;
            Q145=makeQuery(id+"F5.opExtrude","SWEPT_FACE",FACE,{"disambiguationData":[OSD([sQuery(id+"F4.wireOp",EDGE,"E10.sketch_text.stroke-53")])]});
            var Q146;
            Q146=makeQuery(id+"F5.opExtrude","SWEPT_FACE",FACE,{"disambiguationData":[OSD([sQuery(id+"F4.wireOp",EDGE,"E10.sketch_text.stroke-141")])]});
            var Q147;
            Q147=makeQuery(id+"F5.opExtrude","SWEPT_FACE",FACE,{"disambiguationData":[OSD([sQuery(id+"F4.wireOp",EDGE,"E10.sketch_text.stroke-157")])]});
            var Q148;
            Q148=makeQuery(id+"F5.opExtrude","SWEPT_FACE",FACE,{"disambiguationData":[OSD([sQuery(id+"F4.wireOp",EDGE,"E10.sketch_text.stroke-64")])]});
            var Q149;
            Q149=makeQuery(id+"F5.boolean.opBoolean","SPLIT",FACE,{"disambiguationData":[TD([makeQuery(id+"F5.opExtrude","SWEPT_FACE",FACE,{"disambiguationData":[OSD([sQuery(id+"F4.wireOp",EDGE,"E10.sketch_text.stroke-53")])]})])],"derivedFrom":makeQuery(id+"F1.opExtrude","CAP_FACE",FACE,{"disambiguationData":[OSD([sQuery(id+"F0.wireOp",EDGE,"E0.bottom"),sQuery(id+"F0.wireOp",EDGE,"E0.top"),sQuery(id+"F0.wireOp",EDGE,"E0.left"),sQuery(id+"F0.wireOp",EDGE,"E0.right"),sQuery(id+"F0.wireOp",EDGE,"E1"),sQuery(id+"F0.wireOp",EDGE,"E7.MirrorC"),sQuery(id+"F0.wireOp",EDGE,"E8.MirrorC"),sQuery(id+"F0.wireOp",EDGE,"E9.MirrorC")])],"isStart":true})});
            var Q150;
            Q150=makeQuery(id+"F5.opExtrude","SWEPT_FACE",FACE,{"disambiguationData":[OSD([sQuery(id+"F4.wireOp",EDGE,"E10.sketch_text.stroke-36")])]});
            var Q151;
            Q151=makeQuery(id+"F5.opExtrude","SWEPT_FACE",FACE,{"disambiguationData":[OSD([sQuery(id+"F4.wireOp",EDGE,"E10.sketch_text.stroke-22")])]});
            var Q152;
            Q152=makeQuery(id+"F5.boolean.opBoolean","SPLIT",FACE,{"disambiguationData":[TD([makeQuery(id+"F5.opExtrude","SWEPT_FACE",FACE,{"disambiguationData":[OSD([sQuery(id+"F4.wireOp",EDGE,"E10.sketch_text.stroke-119")])]})])],"derivedFrom":makeQuery(id+"F1.opExtrude","CAP_FACE",FACE,{"disambiguationData":[OSD([sQuery(id+"F0.wireOp",EDGE,"E0.bottom"),sQuery(id+"F0.wireOp",EDGE,"E0.top"),sQuery(id+"F0.wireOp",EDGE,"E0.left"),sQuery(id+"F0.wireOp",EDGE,"E0.right"),sQuery(id+"F0.wireOp",EDGE,"E1"),sQuery(id+"F0.wireOp",EDGE,"E7.MirrorC"),sQuery(id+"F0.wireOp",EDGE,"E8.MirrorC"),sQuery(id+"F0.wireOp",EDGE,"E9.MirrorC")])],"isStart":true})});
            var Q153;
            Q153=makeQuery(id+"F5.boolean.opBoolean","SPLIT",FACE,{"disambiguationData":[TD([makeQuery(id+"F5.opExtrude","SWEPT_FACE",FACE,{"disambiguationData":[OSD([sQuery(id+"F4.wireOp",EDGE,"E10.sketch_text.stroke-158")])]})])],"derivedFrom":makeQuery(id+"F1.opExtrude","CAP_FACE",FACE,{"disambiguationData":[OSD([sQuery(id+"F0.wireOp",EDGE,"E0.bottom"),sQuery(id+"F0.wireOp",EDGE,"E0.top"),sQuery(id+"F0.wireOp",EDGE,"E0.left"),sQuery(id+"F0.wireOp",EDGE,"E0.right"),sQuery(id+"F0.wireOp",EDGE,"E1"),sQuery(id+"F0.wireOp",EDGE,"E7.MirrorC"),sQuery(id+"F0.wireOp",EDGE,"E8.MirrorC"),sQuery(id+"F0.wireOp",EDGE,"E9.MirrorC")])],"isStart":true})});
            var Q154;
            Q154=makeQuery(id+"F5.opExtrude","SWEPT_FACE",FACE,{"disambiguationData":[OSD([sQuery(id+"F4.wireOp",EDGE,"E10.sketch_text.stroke-9")])]});
            var Q155;
            Q155=makeQuery(id+"F5.opExtrude","SWEPT_FACE",FACE,{"disambiguationData":[OSD([sQuery(id+"F4.wireOp",EDGE,"E10.sketch_text.stroke-167")])]});
            var Q156;
            Q156=makeQuery(id+"F5.opExtrude","SWEPT_FACE",FACE,{"disambiguationData":[OSD([sQuery(id+"F4.wireOp",EDGE,"E10.sketch_text.stroke-95")])]});
            var Q157;
            Q157=makeQuery(id+"F5.opExtrude","SWEPT_FACE",FACE,{"disambiguationData":[OSD([sQuery(id+"F4.wireOp",EDGE,"E10.sketch_text.stroke-184")])]});
            var Q158;
            Q158=makeQuery(id+"F5.opExtrude","SWEPT_FACE",FACE,{"disambiguationData":[OSD([sQuery(id+"F4.wireOp",EDGE,"E10.sketch_text.stroke-84")])]});
            var Q159;
            Q159=makeQuery(id+"F5.opExtrude","SWEPT_FACE",FACE,{"disambiguationData":[OSD([sQuery(id+"F4.wireOp",EDGE,"E10.sketch_text.stroke-68")])]});
            var Q160;
            Q160=makeQuery(id+"F5.opExtrude","SWEPT_FACE",FACE,{"disambiguationData":[OSD([sQuery(id+"F4.wireOp",EDGE,"E10.sketch_text.stroke-143")])]});
            var Q161;
            Q161=makeQuery(id+"F5.opExtrude","SWEPT_FACE",FACE,{"disambiguationData":[OSD([sQuery(id+"F4.wireOp",EDGE,"E10.sketch_text.stroke-189")])]});
            var Q162;
            Q162=makeQuery(id+"F5.opExtrude","CAP_FACE",FACE,{"disambiguationData":[OSD([sQuery(id+"F4.wireOp",EDGE,"E10.sketch_text.stroke-13"),sQuery(id+"F4.wireOp",EDGE,"E10.sketch_text.stroke-14"),sQuery(id+"F4.wireOp",EDGE,"E10.sketch_text.stroke-15"),sQuery(id+"F4.wireOp",EDGE,"E10.sketch_text.stroke-16"),sQuery(id+"F4.wireOp",EDGE,"E10.sketch_text.stroke-17"),sQuery(id+"F4.wireOp",EDGE,"E10.sketch_text.stroke-18"),sQuery(id+"F4.wireOp",EDGE,"E10.sketch_text.stroke-19"),sQuery(id+"F4.wireOp",EDGE,"E10.sketch_text.stroke-20")])],"isStart":false});
            var Q163;
            Q163=makeQuery(id+"F5.opExtrude","SWEPT_FACE",FACE,{"disambiguationData":[OSD([sQuery(id+"F4.wireOp",EDGE,"E10.sketch_text.stroke-57")])]});
            var Q164;
            Q164=makeQuery(id+"F5.opExtrude","SWEPT_FACE",FACE,{"disambiguationData":[OSD([sQuery(id+"F4.wireOp",EDGE,"E10.sketch_text.stroke-29")])]});
            var Q165;
            Q165=makeQuery(id+"F5.opExtrude","SWEPT_FACE",FACE,{"disambiguationData":[OSD([sQuery(id+"F4.wireOp",EDGE,"E10.sketch_text.stroke-60")])]});
            var Q166;
            Q166=makeQuery(id+"F5.opExtrude","SWEPT_FACE",FACE,{"disambiguationData":[OSD([sQuery(id+"F4.wireOp",EDGE,"E10.sketch_text.stroke-148")])]});
            var Q167;
            Q167=makeQuery(id+"F5.opExtrude","SWEPT_FACE",FACE,{"disambiguationData":[OSD([sQuery(id+"F4.wireOp",EDGE,"E10.sketch_text.stroke-75")])]});
            var Q168;
            Q168=makeQuery(id+"F5.opExtrude","SWEPT_FACE",FACE,{"disambiguationData":[OSD([sQuery(id+"F4.wireOp",EDGE,"E10.sketch_text.stroke-91")])]});
            var Q169;
            Q169=makeQuery(id+"F5.opExtrude","SWEPT_FACE",FACE,{"disambiguationData":[OSD([sQuery(id+"F4.wireOp",EDGE,"E10.sketch_text.stroke-78")])]});
            var Q170;
            Q170=makeQuery(id+"F5.opExtrude","SWEPT_FACE",FACE,{"disambiguationData":[OSD([sQuery(id+"F4.wireOp",EDGE,"E10.sketch_text.stroke-62")])]});
            var Q171;
            Q171=makeQuery(id+"F5.opExtrude","SWEPT_FACE",FACE,{"disambiguationData":[OSD([sQuery(id+"F4.wireOp",EDGE,"E10.sketch_text.stroke-182")])]});
            var Q172;
            Q172=makeQuery(id+"F5.opExtrude","SWEPT_FACE",FACE,{"disambiguationData":[OSD([sQuery(id+"F4.wireOp",EDGE,"E10.sketch_text.stroke-11")])]});
            var Q173;
            Q173=makeQuery(id+"F5.opExtrude","SWEPT_FACE",FACE,{"disambiguationData":[OSD([sQuery(id+"F4.wireOp",EDGE,"E10.sketch_text.stroke-97")])]});
            var Q174;
            Q174=makeQuery(id+"F5.opExtrude","SWEPT_FACE",FACE,{"disambiguationData":[OSD([sQuery(id+"F4.wireOp",EDGE,"E10.sketch_text.stroke-23")])]});
            var Q175;
            Q175=makeQuery(id+"F5.opExtrude","SWEPT_FACE",FACE,{"disambiguationData":[OSD([sQuery(id+"F4.wireOp",EDGE,"E10.sketch_text.stroke-80")])]});
            var Q176;
            Q176=makeQuery(id+"F5.boolean.opBoolean","SPLIT",FACE,{"disambiguationData":[TD([makeQuery(id+"F5.opExtrude","SWEPT_FACE",FACE,{"disambiguationData":[OSD([sQuery(id+"F4.wireOp",EDGE,"E10.sketch_text.stroke-99")])]})])],"derivedFrom":makeQuery(id+"F1.opExtrude","CAP_FACE",FACE,{"disambiguationData":[OSD([sQuery(id+"F0.wireOp",EDGE,"E0.bottom"),sQuery(id+"F0.wireOp",EDGE,"E0.top"),sQuery(id+"F0.wireOp",EDGE,"E0.left"),sQuery(id+"F0.wireOp",EDGE,"E0.right"),sQuery(id+"F0.wireOp",EDGE,"E1"),sQuery(id+"F0.wireOp",EDGE,"E7.MirrorC"),sQuery(id+"F0.wireOp",EDGE,"E8.MirrorC"),sQuery(id+"F0.wireOp",EDGE,"E9.MirrorC")])],"isStart":true})});
            var Q177;
            Q177=makeQuery(id+"F5.opExtrude","SWEPT_FACE",FACE,{"disambiguationData":[OSD([sQuery(id+"F4.wireOp",EDGE,"E10.sketch_text.stroke-168")])]});
            var Q178;
            Q178=makeQuery(id+"F5.opExtrude","SWEPT_FACE",FACE,{"disambiguationData":[OSD([sQuery(id+"F4.wireOp",EDGE,"E10.sketch_text.stroke-188")])]});
            var Q179;
            Q179=makeQuery(id+"F5.opExtrude","SWEPT_FACE",FACE,{"disambiguationData":[OSD([sQuery(id+"F4.wireOp",EDGE,"E10.sketch_text.stroke-129")])]});
            var Q180;
            Q180=makeQuery(id+"F5.opExtrude","SWEPT_FACE",FACE,{"disambiguationData":[OSD([sQuery(id+"F4.wireOp",EDGE,"E10.sketch_text.stroke-27")])]});
            var Q181;
            Q181=makeQuery(id+"F5.opExtrude","SWEPT_FACE",FACE,{"disambiguationData":[OSD([sQuery(id+"F4.wireOp",EDGE,"E10.sketch_text.stroke-175")])]});
            var Q182;
            Q182=makeQuery(id+"F5.opExtrude","SWEPT_FACE",FACE,{"disambiguationData":[OSD([sQuery(id+"F4.wireOp",EDGE,"E10.sketch_text.stroke-42")])]});
            var Q183;
            Q183=makeQuery(id+"F5.opExtrude","SWEPT_FACE",FACE,{"disambiguationData":[OSD([sQuery(id+"F4.wireOp",EDGE,"E10.sketch_text.stroke-118")])]});
            var Q184;
            Q184=makeQuery(id+"F5.opExtrude","SWEPT_FACE",FACE,{"disambiguationData":[OSD([sQuery(id+"F4.wireOp",EDGE,"E10.sketch_text.stroke-151")])]});
            var Q185;
            Q185=makeQuery(id+"F5.opExtrude","SWEPT_FACE",FACE,{"disambiguationData":[OSD([sQuery(id+"F4.wireOp",EDGE,"E10.sketch_text.stroke-137")])]});
            var Q186;
            Q186=makeQuery(id+"F5.opExtrude","SWEPT_FACE",FACE,{"disambiguationData":[OSD([sQuery(id+"F4.wireOp",EDGE,"E10.sketch_text.stroke-83")])]});
            var Q187;
            Q187=makeQuery(id+"F5.boolean.opBoolean","SPLIT",FACE,{"disambiguationData":[TD([makeQuery(id+"F5.opExtrude","SWEPT_FACE",FACE,{"disambiguationData":[OSD([sQuery(id+"F4.wireOp",EDGE,"E10.sketch_text.stroke-90")])]})])],"derivedFrom":makeQuery(id+"F1.opExtrude","CAP_FACE",FACE,{"disambiguationData":[OSD([sQuery(id+"F0.wireOp",EDGE,"E0.bottom"),sQuery(id+"F0.wireOp",EDGE,"E0.top"),sQuery(id+"F0.wireOp",EDGE,"E0.left"),sQuery(id+"F0.wireOp",EDGE,"E0.right"),sQuery(id+"F0.wireOp",EDGE,"E1"),sQuery(id+"F0.wireOp",EDGE,"E7.MirrorC"),sQuery(id+"F0.wireOp",EDGE,"E8.MirrorC"),sQuery(id+"F0.wireOp",EDGE,"E9.MirrorC")])],"isStart":true})});
            var Q188;
            Q188=makeQuery(id+"F5.opExtrude","SWEPT_FACE",FACE,{"disambiguationData":[OSD([sQuery(id+"F4.wireOp",EDGE,"E10.sketch_text.stroke-139")])]});
            var Q189;
            Q189=makeQuery(id+"F5.opExtrude","SWEPT_FACE",FACE,{"disambiguationData":[OSD([sQuery(id+"F4.wireOp",EDGE,"E10.sketch_text.stroke-70")])]});
            var Q190;
            Q190=makeQuery(id+"F5.opExtrude","SWEPT_FACE",FACE,{"disambiguationData":[OSD([sQuery(id+"F4.wireOp",EDGE,"E10.sketch_text.stroke-160")])]});
            var Q191;
            Q191=makeQuery(id+"F5.opExtrude","SWEPT_FACE",FACE,{"disambiguationData":[OSD([sQuery(id+"F4.wireOp",EDGE,"E10.sketch_text.stroke-71")])]});
            var Q192;
            Q192=makeQuery(id+"F5.opExtrude","SWEPT_FACE",FACE,{"disambiguationData":[OSD([sQuery(id+"F4.wireOp",EDGE,"E10.sketch_text.stroke-117")])]});
            var Q193;
            Q193=makeQuery(id+"F5.opExtrude","SWEPT_FACE",FACE,{"disambiguationData":[OSD([sQuery(id+"F4.wireOp",EDGE,"E10.sketch_text.stroke-147")])]});
            var Q194;
            Q194=makeQuery(id+"F5.opExtrude","SWEPT_FACE",FACE,{"disambiguationData":[OSD([sQuery(id+"F4.wireOp",EDGE,"E10.sketch_text.stroke-164")])]});
            var Q195;
            Q195=makeQuery(id+"F5.opExtrude","SWEPT_FACE",FACE,{"disambiguationData":[OSD([sQuery(id+"F4.wireOp",EDGE,"E10.sketch_text.stroke-61")])]});
            var Q196;
            Q196=makeQuery(id+"F5.opExtrude","SWEPT_FACE",FACE,{"disambiguationData":[OSD([sQuery(id+"F4.wireOp",EDGE,"E10.sketch_text.stroke-19")])]});
            var Q197;
            Q197=makeQuery(id+"F5.opExtrude","SWEPT_FACE",FACE,{"disambiguationData":[OSD([sQuery(id+"F4.wireOp",EDGE,"E10.sketch_text.stroke-35")])]});
            var Q198;
            Q198=makeQuery(id+"F5.opExtrude","SWEPT_FACE",FACE,{"disambiguationData":[OSD([sQuery(id+"F4.wireOp",EDGE,"E10.sketch_text.stroke-140")])]});
            var Q199;
            Q199=makeQuery(id+"F5.opExtrude","SWEPT_FACE",FACE,{"disambiguationData":[OSD([sQuery(id+"F4.wireOp",EDGE,"E10.sketch_text.stroke-20")])]});
            var Q200;
            Q200=makeQuery(id+"F5.opExtrude","SWEPT_FACE",FACE,{"disambiguationData":[OSD([sQuery(id+"F4.wireOp",EDGE,"E10.sketch_text.stroke-16")])]});
            var Q201;
            Q201=makeQuery(id+"F5.opExtrude","SWEPT_FACE",FACE,{"disambiguationData":[OSD([sQuery(id+"F4.wireOp",EDGE,"E10.sketch_text.stroke-18")])]});
            var Q202;
            Q202=makeQuery(id+"F5.opExtrude","SWEPT_FACE",FACE,{"disambiguationData":[OSD([sQuery(id+"F4.wireOp",EDGE,"E10.sketch_text.stroke-17")])]});
            var Q203;
            Q203=qCreatedBy(makeId("Right.planeOp"),FACE);
            mirror(context, id + "F6", {"operationType" : NewBodyOperationType.ADD, "entities" : qUnion([Q0]), "faces" : qUnion([Q1, Q2, Q3, Q4, Q5, Q6, Q7, Q8, Q9, Q10, Q11, Q12, Q13, Q14, Q15, Q16, Q17, Q18, Q19, Q20, Q21, Q22, Q23, Q24, Q25, Q26, Q27, Q28, Q29, Q30, Q31, Q32, Q33, Q34, Q35, Q36, Q37, Q38, Q39, Q40, Q41, Q42, Q43, Q44, Q45, Q46, Q47, Q48, Q49, Q50, Q51, Q52, Q53, Q54, Q55, Q56, Q57, Q58, Q59, Q60, Q61, Q62, Q63, Q64, Q65, Q66, Q67, Q68, Q69, Q70, Q71, Q72, Q73, Q74, Q75, Q76, Q77, Q78, Q79, Q80, Q81, Q82, Q83, Q84, Q85, Q86, Q87, Q88, Q89, Q90, Q91, Q92, Q93, Q94, Q95, Q96, Q97, Q98, Q99, Q100, Q101, Q102, Q103, Q104, Q105, Q106, Q107, Q108, Q109, Q110, Q111, Q112, Q113, Q114, Q115, Q116, Q117, Q118, Q119, Q120, Q121, Q122, Q123, Q124, Q125, Q126, Q127, Q128, Q129, Q130, Q131, Q132, Q133, Q134, Q135, Q136, Q137, Q138, Q139, Q140, Q141, Q142, Q143, Q144, Q145, Q146, Q147, Q148, Q149, Q150, Q151, Q152, Q153, Q154, Q155, Q156, Q157, Q158, Q159, Q160, Q161, Q162, Q163, Q164, Q165, Q166, Q167, Q168, Q169, Q170, Q171, Q172, Q173, Q174, Q175, Q176, Q177, Q178, Q179, Q180, Q181, Q182, Q183, Q184, Q185, Q186, Q187, Q188, Q189, Q190, Q191, Q192, Q193, Q194, Q195, Q196, Q197, Q198, Q199, Q200, Q201, Q202]), "mirrorPlane" : qUnion([Q203])});
        }
    });
